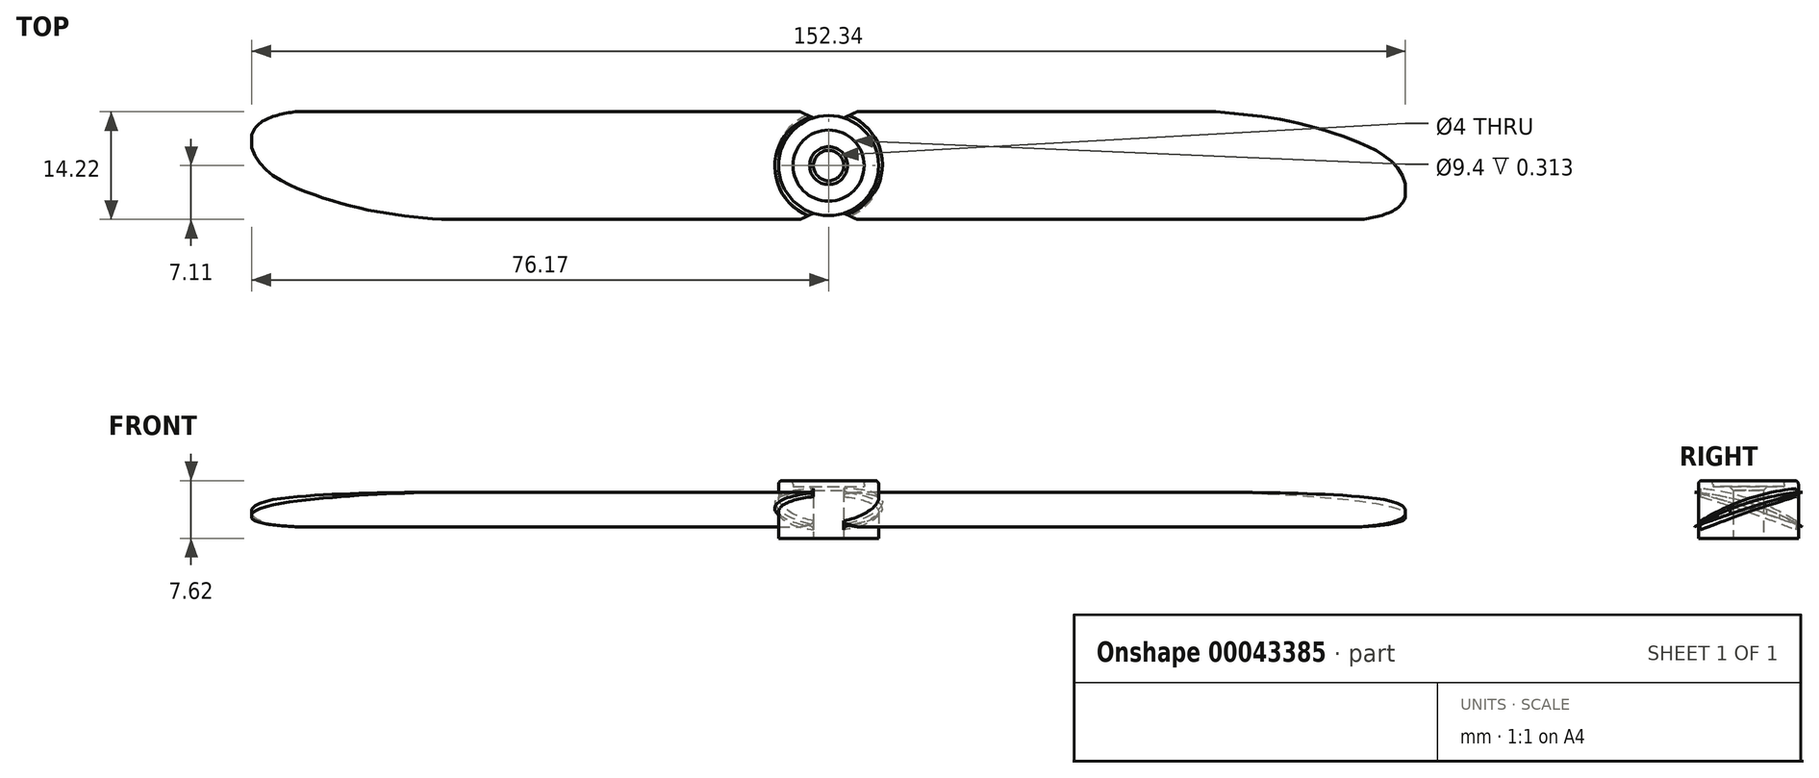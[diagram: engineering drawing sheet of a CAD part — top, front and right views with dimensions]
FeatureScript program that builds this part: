
annotation { "Feature Type Name" : "Feature", "Feature Type Description" : "" }
export const myFeature = defineFeature(function(context is Context, id is Id, definition is map)
    precondition{}
    {
        {
            var Q0;
            Q0=qCreatedBy(makeId("Front.planeOp"),FACE);
            var sketch = newSketch(context, id + "F0", { "sketchPlane" : qUnion([Q0])});
            skLineSegment(sketch, "E0", {"start": v(0, 0) * mm, "end": v(0, 9.6) * mm, "construction": true});
            skLineSegment(sketch, "E1", {"start": v(2, 0) * mm, "end": v(2, 6.8) * mm});
            skLineSegment(sketch, "E2", {"start": v(2, 6.8) * mm, "end": v(4.7, 6.8) * mm});
            skLineSegment(sketch, "E3", {"start": v(4.7, 6.8) * mm, "end": v(4.7, 7.62) * mm});
            skLineSegment(sketch, "E4", {"start": v(4.7, 7.62) * mm, "end": v(6.6, 7.62) * mm});
            skLineSegment(sketch, "E5", {"start": v(6.6, 7.62) * mm, "end": v(6.6, 0) * mm});
            skLineSegment(sketch, "E6", {"start": v(6.6, 0) * mm, "end": v(2, 0) * mm});
            skSolve(sketch);
        }
        {
            var Q0;
            Q0=qSketchRegion(id+"F0",true);
            var Q1;
            Q1=sQuery(id+"F0.wireOp",EDGE,"E0");
            revolve(context, id + "F1", {"entities" : qUnion([Q0]), "axis" : qUnion([Q1]), "revolveType" : RevolveType.FULL});
        }
        {
            var Q0;
            Q0=makeQuery(id+"F1.opRevolve","SWEPT_EDGE",EDGE,{"disambiguationData":[OSD([sQuery(id+"F0.wireOp",EDGE,"E1"),sQuery(id+"F0.wireOp",EDGE,"E2")])]});
            chamfer(context, id + "F2", {"entities" : qUnion([Q0]), "width" : .5 * mm, "tangentPropagation" : true});
        }
        {
            var Q0;
            Q0=makeQuery(id+"F1.opRevolve","SWEPT_EDGE",EDGE,{"disambiguationData":[OSD([sQuery(id+"F0.wireOp",EDGE,"E4"),sQuery(id+"F0.wireOp",EDGE,"E5")])]});
            var Q1;
            Q1=makeQuery(id+"F1.opRevolve","SWEPT_EDGE",EDGE,{"disambiguationData":[OSD([sQuery(id+"F0.wireOp",EDGE,"E3"),sQuery(id+"F0.wireOp",EDGE,"E4")])]});
            fillet(context, id + "F3", {"entities" : qUnion([Q0, Q1]), "radius" : .5 * mm, "tangentPropagation" : true, "allowEdgeOverflow" : false});
        }
        {
            var Q0;
            Q0=qCreatedBy(makeId("Right.planeOp"),FACE);
            cPlane(context, id + "F4", {"entities" : qUnion([Q0]), "cplaneType" : CPlaneType.OFFSET, "offset" : 2 * mm, "width" : 152.4 * mm, "height" : 152.4 * mm});
        }
        {
            var Q0;
            Q0=qCreatedBy(id+"F4.planeOp",FACE);
            var sketch = newSketch(context, id + "F5", { "sketchPlane" : qUnion([Q0])});
            skFitSpline(sketch, "E7", {"points": [v(7.11, 6.1) * mm, v(-7.11, 1.52) * mm], "startDerivative": vector(-15.31, -1.42) * mm, "endDerivative": vector(-14.1, -8.25) * mm});
            skFitSpline(sketch, "E8", {"points": [v(7.11, 6.1) * mm, v(-7.11, 1.52) * mm], "startDerivative": vector(-15.85, -4.38) * mm, "endDerivative": vector(-15.17, -5.64) * mm});
            skSolve(sketch);
        }
        {
            var Q0;
            Q0=qSketchRegion(id+"F5",true);
            extrude(context, id + "F6", {"entities" : qUnion([Q0]), "depth" : 74.17 * mm});
        }
        {
            var Q0;
            Q0=qCreatedBy(makeId("Top.planeOp"),FACE);
            var sketch = newSketch(context, id + "F7", { "sketchPlane" : qUnion([Q0])});
            skLineSegment(sketch, "E9", {"start": v(2, 6.3) * mm, "end": v(4.8, 7.6) * mm});
            skLineSegment(sketch, "E10", {"start": v(4.8, 7.6) * mm, "end": v(44.45, 7.6) * mm});
            skFitSpline(sketch, "E11", {"points": [v(44.45, 7.6) * mm, v(65.38, 4.68) * mm, v(74.87, 0) * mm, v(75.78, -4.92) * mm, v(52.06, -7.52) * mm], "startDerivative": vector(127.56, -8.25) * mm, "endDerivative": vector(-120.05, 0.74) * mm});
            skLineSegment(sketch, "E12", {"start": v(52.06, -7.52) * mm, "end": v(4.63, -7.52) * mm});
            skLineSegment(sketch, "E13", {"start": v(4.63, -7.52) * mm, "end": v(2, -6.3) * mm});
            skLineSegment(sketch, "E14", {"start": v(2, -6.3) * mm, "end": v(0.7, -9.1) * mm});
            skLineSegment(sketch, "E15", {"start": v(0.7, -9.1) * mm, "end": v(79.12, -9.1) * mm});
            skLineSegment(sketch, "E16", {"start": v(79.12, -9.1) * mm, "end": v(79.12, 10.53) * mm});
            skLineSegment(sketch, "E17", {"start": v(79.12, 10.53) * mm, "end": v(0.95, 10.53) * mm});
            skLineSegment(sketch, "E18", {"start": v(0.95, 10.53) * mm, "end": v(2, 6.3) * mm});
            skSolve(sketch);
        }
        {
            var Q0;
            Q0=qSketchRegion(id+"F7",true);
            extrude(context, id + "F8", {"entities" : qUnion([Q0]), "operationType" : NewBodyOperationType.REMOVE, "endBound" : BoundingType.THROUGH_ALL, "depth" : 25.4 * mm});
        }
        {
            var Q0;
            Q0=makeQuery(id+"F6.opExtrude","SWEPT_BODY",BODY,{"disambiguationData":[OSD([sQuery(id+"F5.wireOp",EDGE,"E7"),sQuery(id+"F5.wireOp",EDGE,"E8")])]});
            var Q1;
            Q1=sQuery(id+"F0.wireOp",EDGE,"E0");
            circularPattern(context, id + "F9", {"entities" : qUnion([Q0]), "axis" : qUnion([Q1]), "angle" : 180 * degree, "instanceCount" : 2});
        }
        {
            var Q0;
            Q0=makeQuery(id+"F1.opRevolve","SWEPT_BODY",BODY,{"disambiguationData":[OSD([sQuery(id+"F0.wireOp",EDGE,"E1"),sQuery(id+"F0.wireOp",EDGE,"E2"),sQuery(id+"F0.wireOp",EDGE,"E3"),sQuery(id+"F0.wireOp",EDGE,"E4"),sQuery(id+"F0.wireOp",EDGE,"E5"),sQuery(id+"F0.wireOp",EDGE,"E6")])]});
            var Q1;
            Q1=makeQuery(id+"F6.opExtrude","SWEPT_BODY",BODY,{"disambiguationData":[OSD([sQuery(id+"F5.wireOp",EDGE,"E7"),sQuery(id+"F5.wireOp",EDGE,"E8")])]});
            var Q2;
            Q2=makeQuery(id+"F9.opPattern","COPY",BODY,{"derivedFrom":makeQuery(id+"F6.opExtrude","SWEPT_BODY",BODY,{"disambiguationData":[OSD([sQuery(id+"F5.wireOp",EDGE,"E7"),sQuery(id+"F5.wireOp",EDGE,"E8")])]}),"instanceName":"1"});
            booleanBodies(context, id + "F10", {"operationType" : BooleanOperationType.UNION, "tools" : qUnion([Q0, Q1, Q2])});
        }
        {
            var Q0;
            Q0=makeQuery(id+"F10.opBoolean","INTERSECT",EDGE,{"derivedFrom":[makeQuery(id+"F1.opRevolve","SWEPT_FACE",FACE,{"disambiguationData":[OSD([sQuery(id+"F0.wireOp",EDGE,"E5")])]}),makeQuery(id+"F6.opExtrude","SWEPT_FACE",FACE,{"disambiguationData":[OSD([sQuery(id+"F5.wireOp",EDGE,"E7")])]})]});
            var Q1;
            Q1=makeQuery(id+"F10.opBoolean","INTERSECT",EDGE,{"derivedFrom":[makeQuery(id+"F1.opRevolve","SWEPT_FACE",FACE,{"disambiguationData":[OSD([sQuery(id+"F0.wireOp",EDGE,"E5")])]}),makeQuery(id+"F6.opExtrude","SWEPT_FACE",FACE,{"disambiguationData":[OSD([sQuery(id+"F5.wireOp",EDGE,"E8")])]})]});
            var Q2;
            Q2=makeQuery(id+"F10.opBoolean","INTERSECT",EDGE,{"derivedFrom":[makeQuery(id+"F1.opRevolve","SWEPT_FACE",FACE,{"disambiguationData":[OSD([sQuery(id+"F0.wireOp",EDGE,"E5")])]}),makeQuery(id+"F9.opPattern","COPY",FACE,{"derivedFrom":makeQuery(id+"F6.opExtrude","SWEPT_FACE",FACE,{"disambiguationData":[OSD([sQuery(id+"F5.wireOp",EDGE,"E7")])]}),"instanceName":"1"})]});
            var Q3;
            Q3=makeQuery(id+"F10.opBoolean","INTERSECT",EDGE,{"derivedFrom":[makeQuery(id+"F1.opRevolve","SWEPT_FACE",FACE,{"disambiguationData":[OSD([sQuery(id+"F0.wireOp",EDGE,"E5")])]}),makeQuery(id+"F9.opPattern","COPY",FACE,{"derivedFrom":makeQuery(id+"F6.opExtrude","SWEPT_FACE",FACE,{"disambiguationData":[OSD([sQuery(id+"F5.wireOp",EDGE,"E8")])]}),"instanceName":"1"})]});
            fillet(context, id + "F11", {"entities" : qUnion([Q0, Q1, Q2, Q3]), "radius" : .5 * mm, "tangentPropagation" : true, "allowEdgeOverflow" : false});
        }
    });
